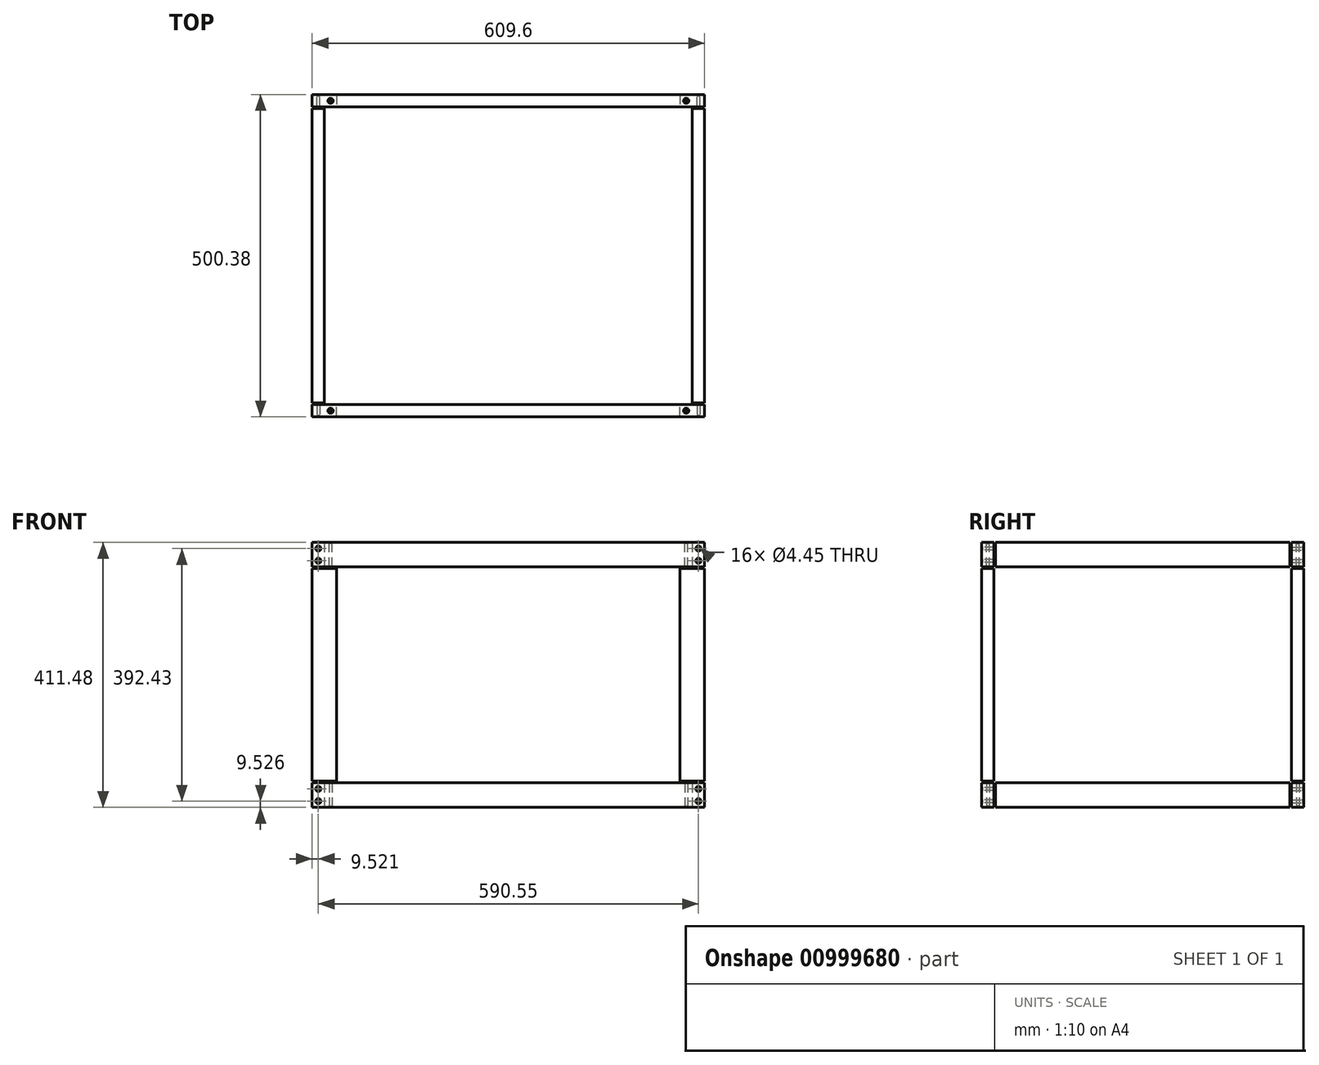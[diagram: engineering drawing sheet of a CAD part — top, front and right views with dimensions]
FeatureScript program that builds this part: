
annotation { "Feature Type Name" : "Feature", "Feature Type Description" : "" }
export const myFeature = defineFeature(function(context is Context, id is Id, definition is map)
    precondition{}
    {
        {
            var Q0;
            Q0=qCreatedBy(makeId("Front.planeOp"),FACE);
            var sketch = newSketch(context, id + "F0", { "sketchPlane" : qUnion([Q0])});
            skLineSegment(sketch, "E0.bottom", {"start": v(-520.32, 23.41) * mm, "end": v(89.28, 23.41) * mm});
            skLineSegment(sketch, "E0.top", {"start": v(-520.32, -14.69) * mm, "end": v(89.28, -14.69) * mm});
            skLineSegment(sketch, "E0.left", {"start": v(-520.32, 23.41) * mm, "end": v(-520.32, -14.69) * mm});
            skLineSegment(sketch, "E0.right", {"start": v(89.28, 23.41) * mm, "end": v(89.28, -14.69) * mm});
            skLineSegment(sketch, "E1.bottom", {"start": v(-520.32, -17.23) * mm, "end": v(-482.22, -17.23) * mm});
            skLineSegment(sketch, "E1.top", {"start": v(-520.32, -347.43) * mm, "end": v(-482.22, -347.43) * mm});
            skLineSegment(sketch, "E1.left", {"start": v(-520.32, -17.23) * mm, "end": v(-520.32, -347.43) * mm});
            skLineSegment(sketch, "E1.right", {"start": v(-482.22, -17.23) * mm, "end": v(-482.22, -347.43) * mm});
            skLineSegment(sketch, "E2.bottom", {"start": v(89.28, -17.23) * mm, "end": v(51.18, -17.23) * mm});
            skLineSegment(sketch, "E2.top", {"start": v(89.28, -347.43) * mm, "end": v(51.18, -347.43) * mm});
            skLineSegment(sketch, "E2.left", {"start": v(89.28, -17.23) * mm, "end": v(89.28, -347.43) * mm});
            skLineSegment(sketch, "E2.right", {"start": v(51.18, -17.23) * mm, "end": v(51.18, -347.43) * mm});
            skLineSegment(sketch, "E3.bottom", {"start": v(-520.32, -388.07) * mm, "end": v(89.28, -388.07) * mm});
            skLineSegment(sketch, "E3.top", {"start": v(-520.32, -349.97) * mm, "end": v(89.28, -349.97) * mm});
            skLineSegment(sketch, "E3.left", {"start": v(-520.32, -388.07) * mm, "end": v(-520.32, -349.97) * mm});
            skLineSegment(sketch, "E3.right", {"start": v(89.28, -388.07) * mm, "end": v(89.28, -349.97) * mm});
            skSolve(sketch);
        }
        {
            var Q0;
            Q0=makeQuery(id+"F0.imprint","IMPRINT",FACE,{"disambiguationData":[TD([[makeQuery(id+"F0.imprint","IMPRINT",EDGE,{"derivedFrom":sQuery(id+"F0.wireOp",EDGE,"E1.bottom")}),-1.0]])]});
            var Q1;
            Q1=makeQuery(id+"F0.imprint","IMPRINT",FACE,{"disambiguationData":[TD([[makeQuery(id+"F0.imprint","IMPRINT",EDGE,{"derivedFrom":sQuery(id+"F0.wireOp",EDGE,"E0.bottom")}),-1.0]])]});
            var Q2;
            Q2=makeQuery(id+"F0.imprint","IMPRINT",FACE,{"disambiguationData":[TD([[makeQuery(id+"F0.imprint","IMPRINT",EDGE,{"derivedFrom":sQuery(id+"F0.wireOp",EDGE,"E2.bottom")}),1.0]])]});
            var Q3;
            Q3=makeQuery(id+"F0.imprint","IMPRINT",FACE,{"disambiguationData":[TD([[makeQuery(id+"F0.imprint","IMPRINT",EDGE,{"derivedFrom":sQuery(id+"F0.wireOp",EDGE,"E3.bottom")}),1.0]])]});
            extrude(context, id + "F1", {"entities" : qUnion([Q0, Q1, Q2, Q3]), "depth" : 19.05 * mm, "offsetDistance" : 25.4 * mm});
        }
        {
            var Q0;
            Q0=makeQuery(id+"F1.opExtrude","SWEPT_FACE",FACE,{"disambiguationData":[OSD([sQuery(id+"F0.wireOp",EDGE,"E0.right")])]});
            var sketch = newSketch(context, id + "F2", { "sketchPlane" : qUnion([Q0])});
            skLineSegment(sketch, "E4.bottom", {"start": v(2.54, 23.41) * mm, "end": v(459.74, 23.41) * mm});
            skLineSegment(sketch, "E4.top", {"start": v(2.54, -14.69) * mm, "end": v(459.74, -14.69) * mm});
            skLineSegment(sketch, "E4.left", {"start": v(2.54, 23.41) * mm, "end": v(2.54, -14.69) * mm});
            skLineSegment(sketch, "E4.right", {"start": v(459.74, 23.41) * mm, "end": v(459.74, -14.69) * mm});
            skLineSegment(sketch, "E5.0", {"start": v(-19.05, -349.97) * mm, "end": v(0, -349.97) * mm, "construction": true});
            skLineSegment(sketch, "E6.bottom", {"start": v(2.54, -349.97) * mm, "end": v(459.74, -349.97) * mm});
            skLineSegment(sketch, "E6.top", {"start": v(2.54, -388.07) * mm, "end": v(459.74, -388.07) * mm});
            skLineSegment(sketch, "E6.left", {"start": v(2.54, -349.97) * mm, "end": v(2.54, -388.07) * mm});
            skLineSegment(sketch, "E6.right", {"start": v(459.74, -349.97) * mm, "end": v(459.74, -388.07) * mm});
            skSolve(sketch);
        }
        {
            var Q0;
            Q0=makeQuery(id+"F2.imprint","IMPRINT",FACE,{"disambiguationData":[TD([[makeQuery(id+"F2.imprint","IMPRINT",EDGE,{"derivedFrom":sQuery(id+"F2.wireOp",EDGE,"E4.bottom")}),-1.0]])]});
            var Q1;
            Q1=makeQuery(id+"F2.imprint","IMPRINT",FACE,{"disambiguationData":[TD([[makeQuery(id+"F2.imprint","IMPRINT",EDGE,{"derivedFrom":sQuery(id+"F2.wireOp",EDGE,"E6.bottom")}),-1.0]])]});
            extrude(context, id + "F3", {"entities" : qUnion([Q0, Q1]), "oppositeDirection" : true, "depth" : 19.05 * mm, "offsetDistance" : 25.4 * mm});
        }
        {
            var Q0;
            Q0=makeQuery(id+"F3.opExtrude","SWEPT_FACE",FACE,{"disambiguationData":[OSD([sQuery(id+"F2.wireOp",EDGE,"E4.right")])]});
            cPlane(context, id + "F4", {"entities" : qUnion([Q0]), "cplaneType" : CPlaneType.OFFSET, "offset" : 2.54 * mm, "width" : 152.4 * mm, "height" : 152.4 * mm});
        }
        {
            var Q0;
            Q0=qCreatedBy(id+"F4.planeOp",FACE);
            var sketch = newSketch(context, id + "F5", { "sketchPlane" : qUnion([Q0])});
            skLineSegment(sketch, "E7.0", {"start": v(-89.28, 23.41) * mm, "end": v(-89.28, -14.69) * mm});
            skLineSegment(sketch, "E7.1", {"start": v(-89.28, -349.97) * mm, "end": v(-89.28, -388.07) * mm});
            skLineSegment(sketch, "E8", {"start": v(-89.28, 23.41) * mm, "end": v(520.32, 23.41) * mm});
            skLineSegment(sketch, "E9", {"start": v(520.32, 23.41) * mm, "end": v(520.32, -14.69) * mm});
            skLineSegment(sketch, "E10", {"start": v(520.32, -14.69) * mm, "end": v(-89.28, -14.69) * mm});
            skLineSegment(sketch, "E11", {"start": v(-89.28, -349.97) * mm, "end": v(520.32, -349.97) * mm});
            skLineSegment(sketch, "E12", {"start": v(520.32, -349.97) * mm, "end": v(520.32, -388.07) * mm});
            skLineSegment(sketch, "E13", {"start": v(520.32, -388.07) * mm, "end": v(-89.28, -388.07) * mm});
            skLineSegment(sketch, "E14.0", {"start": v(-89.28, -17.23) * mm, "end": v(-51.18, -17.23) * mm});
            skLineSegment(sketch, "E14.1", {"start": v(520.32, -17.23) * mm, "end": v(482.22, -17.23) * mm});
            skLineSegment(sketch, "E15", {"start": v(-51.18, -17.23) * mm, "end": v(-51.18, -347.43) * mm});
            skLineSegment(sketch, "E16", {"start": v(-51.18, -347.43) * mm, "end": v(-89.28, -347.43) * mm});
            skLineSegment(sketch, "E17", {"start": v(-89.28, -347.43) * mm, "end": v(-89.28, -17.23) * mm});
            skLineSegment(sketch, "E18", {"start": v(482.22, -17.23) * mm, "end": v(482.22, -347.43) * mm});
            skLineSegment(sketch, "E19", {"start": v(482.22, -347.43) * mm, "end": v(520.32, -347.43) * mm});
            skLineSegment(sketch, "E20", {"start": v(520.32, -347.43) * mm, "end": v(520.32, -17.23) * mm});
            skSolve(sketch);
        }
        {
            var Q0;
            Q0=makeQuery(id+"F5.imprint","IMPRINT",FACE,{"disambiguationData":[TD([[makeQuery(id+"F5.imprint","IMPRINT",EDGE,{"derivedFrom":sQuery(id+"F5.wireOp",EDGE,"E7.0")}),1.0]])]});
            var Q1;
            Q1=makeQuery(id+"F5.imprint","IMPRINT",FACE,{"disambiguationData":[TD([[makeQuery(id+"F5.imprint","IMPRINT",EDGE,{"derivedFrom":sQuery(id+"F5.wireOp",EDGE,"E14.1")}),1.0]])]});
            var Q2;
            Q2=makeQuery(id+"F5.imprint","IMPRINT",FACE,{"disambiguationData":[TD([[makeQuery(id+"F5.imprint","IMPRINT",EDGE,{"derivedFrom":sQuery(id+"F5.wireOp",EDGE,"E7.1")}),1.0]])]});
            var Q3;
            Q3=makeQuery(id+"F5.imprint","IMPRINT",FACE,{"disambiguationData":[TD([[makeQuery(id+"F5.imprint","IMPRINT",EDGE,{"derivedFrom":sQuery(id+"F5.wireOp",EDGE,"E14.0")}),-1.0]])]});
            extrude(context, id + "F6", {"entities" : qUnion([Q0, Q1, Q2, Q3]), "depth" : 19.05 * mm, "offsetDistance" : 25.4 * mm});
        }
        {
            var Q0;
            Q0=makeQuery(id+"F6.opExtrude","SWEPT_FACE",FACE,{"disambiguationData":[OSD([sQuery(id+"F5.wireOp",EDGE,"E9")])]});
            var sketch = newSketch(context, id + "F7", { "sketchPlane" : qUnion([Q0])});
            skLineSegment(sketch, "E21.0", {"start": v(-462.28, 23.41) * mm, "end": v(-462.28, -14.69) * mm, "construction": true});
            skLineSegment(sketch, "E21.1", {"start": v(-462.28, -349.97) * mm, "end": v(-462.28, -388.07) * mm, "construction": true});
            skLineSegment(sketch, "E22.0", {"start": v(-459.74, -349.97) * mm, "end": v(-459.74, -388.07) * mm});
            skLineSegment(sketch, "E23.0", {"start": v(-459.74, 23.41) * mm, "end": v(-459.74, -14.69) * mm});
            skLineSegment(sketch, "E24", {"start": v(-459.74, 23.41) * mm, "end": v(-2.54, 23.41) * mm});
            skLineSegment(sketch, "E25", {"start": v(-2.54, 23.41) * mm, "end": v(-2.54, -14.69) * mm});
            skLineSegment(sketch, "E26", {"start": v(-2.54, -14.69) * mm, "end": v(-459.74, -14.69) * mm});
            skLineSegment(sketch, "E27", {"start": v(-459.74, -349.97) * mm, "end": v(-2.54, -349.97) * mm});
            skLineSegment(sketch, "E28", {"start": v(-2.54, -349.97) * mm, "end": v(-2.54, -388.07) * mm});
            skLineSegment(sketch, "E29", {"start": v(-2.54, -388.07) * mm, "end": v(-459.74, -388.07) * mm});
            skSolve(sketch);
        }
        {
            var Q0;
            Q0=makeQuery(id+"F7.imprint","IMPRINT",FACE,{"disambiguationData":[TD([[makeQuery(id+"F7.imprint","IMPRINT",EDGE,{"derivedFrom":sQuery(id+"F7.wireOp",EDGE,"E23.0")}),1.0]])]});
            var Q1;
            Q1=makeQuery(id+"F7.imprint","IMPRINT",FACE,{"disambiguationData":[TD([[makeQuery(id+"F7.imprint","IMPRINT",EDGE,{"derivedFrom":sQuery(id+"F7.wireOp",EDGE,"E22.0")}),1.0]])]});
            extrude(context, id + "F8", {"entities" : qUnion([Q0, Q1]), "oppositeDirection" : true, "depth" : 19.05 * mm, "offsetDistance" : 25.4 * mm});
        }
        {
            var Q0;
            Q0=makeQuery(id+"F1.opExtrude","SWEPT_FACE",FACE,{"disambiguationData":[OSD([sQuery(id+"F0.wireOp",EDGE,"E0.bottom")])]});
            var sketch = newSketch(context, id + "F9", { "sketchPlane" : qUnion([Q0])});
            skLineSegment(sketch, "E30.0", {"start": v(-520.32, -19.05) * mm, "end": v(-520.32, 0) * mm, "construction": true});
            skPoint(sketch, "E31", {"position": v(-491.75, -9.53) * mm});
            skPoint(sketch, "E31.positionSnap0", {"position": v(-520.32, -9.53) * mm});
            skLineSegment(sketch, "E32", {"start": v(-215.52, 0) * mm, "end": v(-215.52, -19.05) * mm, "construction": true});
            skLineSegment(sketch, "E33.0", {"start": v(-520.32, 459.74) * mm, "end": v(-520.32, 2.54) * mm, "construction": true});
            skLineSegment(sketch, "E34", {"start": v(-520.32, 231.14) * mm, "end": v(-501.27, 231.14) * mm, "construction": true});
            skPoint(sketch, "E35.MirrorP", {"position": v(60.7, -9.53) * mm});
            skPoint(sketch, "E36.MirrorP", {"position": v(-491.75, 471.8) * mm});
            skPoint(sketch, "E37.MirrorP", {"position": v(60.7, 471.8) * mm});
            skSolve(sketch);
        }
        {
            var Q0;
            Q0=sQuery(id+"F9.wireOp",VERTEX,"E31");
            var Q1;
            Q1=sQuery(id+"F9.wireOp",VERTEX,"E35.MirrorP");
            var Q2;
            Q2=sQuery(id+"F9.wireOp",VERTEX,"E37.MirrorP");
            var Q3;
            Q3=sQuery(id+"F9.wireOp",VERTEX,"E36.MirrorP");
            var Q4;
            Q4=makeQuery(id+"F6.opExtrude","SWEPT_BODY",BODY,{"disambiguationData":[OSD([sQuery(id+"F5.wireOp",EDGE,"E7.0"),sQuery(id+"F5.wireOp",EDGE,"E8"),sQuery(id+"F5.wireOp",EDGE,"E9"),sQuery(id+"F5.wireOp",EDGE,"E10")])]});
            var Q5;
            Q5=makeQuery(id+"F1.opExtrude","SWEPT_BODY",BODY,{"disambiguationData":[OSD([sQuery(id+"F0.wireOp",EDGE,"E0.bottom"),sQuery(id+"F0.wireOp",EDGE,"E0.top"),sQuery(id+"F0.wireOp",EDGE,"E0.left"),sQuery(id+"F0.wireOp",EDGE,"E0.right")])]});
            hole(context, id + "F10", {"style" : HoleStyle.C_SINK, "endStyle" : HoleEndStyle.THROUGH, "holeDiameter" : 4.44 * mm, "cSinkDiameter" : 8.13 * mm, "cSinkAngle" : 82 * degree, "majorDiameter" : 6.35 * mm, "isTappedThrough" : true, "tappedDepth" : 12.7 * mm, "tapClearance" : 3, "startFromSketch" : true, "locations" : qUnion([Q0, Q1, Q2, Q3]), "scope" : qUnion([Q4, Q5])});
        }
        {
            var Q0;
            Q0=makeQuery(id+"F1.opExtrude","SWEPT_FACE",FACE,{"disambiguationData":[OSD([sQuery(id+"F0.wireOp",EDGE,"E3.bottom")])]});
            var sketch = newSketch(context, id + "F11", { "sketchPlane" : qUnion([Q0])});
            skPoint(sketch, "E38.0", {"position": v(-491.75, 9.53) * mm});
            skPoint(sketch, "E38.1", {"position": v(60.7, 9.53) * mm});
            skPoint(sketch, "E38.2", {"position": v(60.7, -471.8) * mm});
            skPoint(sketch, "E38.3", {"position": v(-491.75, -471.8) * mm});
            skSolve(sketch);
        }
        {
            var Q0;
            Q0=sQuery(id+"F11.wireOp",VERTEX,"E38.0");
            var Q1;
            Q1=sQuery(id+"F11.wireOp",VERTEX,"E38.1");
            var Q2;
            Q2=sQuery(id+"F11.wireOp",VERTEX,"E38.3");
            var Q3;
            Q3=sQuery(id+"F11.wireOp",VERTEX,"E38.2");
            var Q4;
            Q4=makeQuery(id+"F1.opExtrude","SWEPT_BODY",BODY,{"disambiguationData":[OSD([sQuery(id+"F0.wireOp",EDGE,"E3.bottom"),sQuery(id+"F0.wireOp",EDGE,"E3.top"),sQuery(id+"F0.wireOp",EDGE,"E3.left"),sQuery(id+"F0.wireOp",EDGE,"E3.right")])]});
            var Q5;
            Q5=makeQuery(id+"F6.opExtrude","SWEPT_BODY",BODY,{"disambiguationData":[OSD([sQuery(id+"F5.wireOp",EDGE,"E7.1"),sQuery(id+"F5.wireOp",EDGE,"E11"),sQuery(id+"F5.wireOp",EDGE,"E12"),sQuery(id+"F5.wireOp",EDGE,"E13")])]});
            hole(context, id + "F12", {"style" : HoleStyle.C_SINK, "endStyle" : HoleEndStyle.THROUGH, "holeDiameter" : 4.44 * mm, "cSinkDiameter" : 8.13 * mm, "cSinkAngle" : 82 * degree, "majorDiameter" : 6.35 * mm, "isTappedThrough" : true, "tappedDepth" : 12.7 * mm, "tapClearance" : 3, "startFromSketch" : true, "locations" : qUnion([Q0, Q1, Q2, Q3]), "scope" : qUnion([Q4, Q5])});
        }
        {
            var Q0;
            Q0=makeQuery(id+"F6.opExtrude","CAP_FACE",FACE,{"disambiguationData":[OSD([sQuery(id+"F5.wireOp",EDGE,"E7.1"),sQuery(id+"F5.wireOp",EDGE,"E11"),sQuery(id+"F5.wireOp",EDGE,"E12"),sQuery(id+"F5.wireOp",EDGE,"E13")])],"isStart":false});
            var sketch = newSketch(context, id + "F13", { "sketchPlane" : qUnion([Q0])});
            skLineSegment(sketch, "E39.0", {"start": v(520.32, -349.97) * mm, "end": v(520.32, -388.07) * mm, "construction": true});
            skPoint(sketch, "E40", {"position": v(510.8, -378.54) * mm});
            skPoint(sketch, "E41", {"position": v(510.8, -359.5) * mm});
            skLineSegment(sketch, "E42.0", {"start": v(520.32, -347.43) * mm, "end": v(520.32, -17.23) * mm, "construction": true});
            skLineSegment(sketch, "E42.1", {"start": v(520.32, -388.07) * mm, "end": v(-89.28, -388.07) * mm, "construction": true});
            skLineSegment(sketch, "E43", {"start": v(215.52, -388.07) * mm, "end": v(215.52, -349.97) * mm, "construction": true});
            skLineSegment(sketch, "E44", {"start": v(520.32, -182.33) * mm, "end": v(482.22, -182.33) * mm, "construction": true});
            skPoint(sketch, "E45.MirrorP", {"position": v(-79.75, -359.5) * mm});
            skPoint(sketch, "E46.MirrorP", {"position": v(-79.75, -378.54) * mm});
            skPoint(sketch, "E47.MirrorP", {"position": v(510.8, -5.16) * mm});
            skPoint(sketch, "E48.MirrorP", {"position": v(510.8, 13.89) * mm});
            skPoint(sketch, "E49.MirrorP", {"position": v(-79.75, -5.16) * mm});
            skPoint(sketch, "E50.MirrorP", {"position": v(-79.75, 13.89) * mm});
            skSolve(sketch);
        }
        {
            var Q0;
            Q0=sQuery(id+"F13.wireOp",VERTEX,"E40");
            var Q1;
            Q1=sQuery(id+"F13.wireOp",VERTEX,"E41");
            var Q2;
            Q2=sQuery(id+"F13.wireOp",VERTEX,"E46.MirrorP");
            var Q3;
            Q3=sQuery(id+"F13.wireOp",VERTEX,"E45.MirrorP");
            var Q4;
            Q4=sQuery(id+"F13.wireOp",VERTEX,"E49.MirrorP");
            var Q5;
            Q5=sQuery(id+"F13.wireOp",VERTEX,"E50.MirrorP");
            var Q6;
            Q6=sQuery(id+"F13.wireOp",VERTEX,"E47.MirrorP");
            var Q7;
            Q7=sQuery(id+"F13.wireOp",VERTEX,"E48.MirrorP");
            var Q8;
            Q8=makeQuery(id+"F6.opExtrude","SWEPT_BODY",BODY,{"disambiguationData":[OSD([sQuery(id+"F5.wireOp",EDGE,"E7.1"),sQuery(id+"F5.wireOp",EDGE,"E11"),sQuery(id+"F5.wireOp",EDGE,"E12"),sQuery(id+"F5.wireOp",EDGE,"E13")])]});
            var Q9;
            Q9=makeQuery(id+"F6.opExtrude","SWEPT_BODY",BODY,{"disambiguationData":[OSD([sQuery(id+"F5.wireOp",EDGE,"E7.0"),sQuery(id+"F5.wireOp",EDGE,"E8"),sQuery(id+"F5.wireOp",EDGE,"E9"),sQuery(id+"F5.wireOp",EDGE,"E10")])]});
            hole(context, id + "F14", {"style" : HoleStyle.C_SINK, "endStyle" : HoleEndStyle.THROUGH, "holeDiameter" : 4.44 * mm, "cSinkDiameter" : 8.13 * mm, "cSinkAngle" : 82 * degree, "majorDiameter" : 6.35 * mm, "isTappedThrough" : true, "tappedDepth" : 12.7 * mm, "tapClearance" : 3, "startFromSketch" : true, "locations" : qUnion([Q0, Q1, Q2, Q3, Q4, Q5, Q6, Q7]), "scope" : qUnion([Q8, Q9])});
        }
        {
            var Q0;
            Q0=makeQuery(id+"F1.opExtrude","CAP_FACE",FACE,{"disambiguationData":[OSD([sQuery(id+"F0.wireOp",EDGE,"E3.bottom"),sQuery(id+"F0.wireOp",EDGE,"E3.top"),sQuery(id+"F0.wireOp",EDGE,"E3.left"),sQuery(id+"F0.wireOp",EDGE,"E3.right")])],"isStart":false});
            var sketch = newSketch(context, id + "F15", { "sketchPlane" : qUnion([Q0])});
            skPoint(sketch, "E51.0", {"position": v(79.75, -378.54) * mm});
            skPoint(sketch, "E51.1", {"position": v(79.75, -359.5) * mm});
            skPoint(sketch, "E51.2", {"position": v(-510.8, -378.54) * mm});
            skPoint(sketch, "E51.3", {"position": v(-510.8, -359.5) * mm});
            skPoint(sketch, "E51.4", {"position": v(-510.8, -5.16) * mm});
            skPoint(sketch, "E51.5", {"position": v(-510.8, 13.89) * mm});
            skPoint(sketch, "E51.6", {"position": v(79.75, -5.16) * mm});
            skPoint(sketch, "E51.7", {"position": v(79.75, 13.89) * mm});
            skSolve(sketch);
        }
        {
            var Q0;
            Q0=sQuery(id+"F15.wireOp",VERTEX,"E51.0");
            var Q1;
            Q1=sQuery(id+"F15.wireOp",VERTEX,"E51.1");
            var Q2;
            Q2=sQuery(id+"F15.wireOp",VERTEX,"E51.2");
            var Q3;
            Q3=sQuery(id+"F15.wireOp",VERTEX,"E51.3");
            var Q4;
            Q4=sQuery(id+"F15.wireOp",VERTEX,"E51.5");
            var Q5;
            Q5=sQuery(id+"F15.wireOp",VERTEX,"E51.4");
            var Q6;
            Q6=sQuery(id+"F15.wireOp",VERTEX,"E51.7");
            var Q7;
            Q7=sQuery(id+"F15.wireOp",VERTEX,"E51.6");
            var Q8;
            Q8=makeQuery(id+"F1.opExtrude","SWEPT_BODY",BODY,{"disambiguationData":[OSD([sQuery(id+"F0.wireOp",EDGE,"E3.bottom"),sQuery(id+"F0.wireOp",EDGE,"E3.top"),sQuery(id+"F0.wireOp",EDGE,"E3.left"),sQuery(id+"F0.wireOp",EDGE,"E3.right")])]});
            var Q9;
            Q9=makeQuery(id+"F1.opExtrude","SWEPT_BODY",BODY,{"disambiguationData":[OSD([sQuery(id+"F0.wireOp",EDGE,"E0.bottom"),sQuery(id+"F0.wireOp",EDGE,"E0.top"),sQuery(id+"F0.wireOp",EDGE,"E0.left"),sQuery(id+"F0.wireOp",EDGE,"E0.right")])]});
            hole(context, id + "F16", {"style" : HoleStyle.C_SINK, "endStyle" : HoleEndStyle.THROUGH, "holeDiameter" : 4.44 * mm, "cSinkDiameter" : 8.13 * mm, "cSinkAngle" : 82 * degree, "majorDiameter" : 6.35 * mm, "isTappedThrough" : true, "tappedDepth" : 12.7 * mm, "tapClearance" : 3, "startFromSketch" : true, "locations" : qUnion([Q0, Q1, Q2, Q3, Q4, Q5, Q6, Q7]), "scope" : qUnion([Q8, Q9])});
        }
    });
